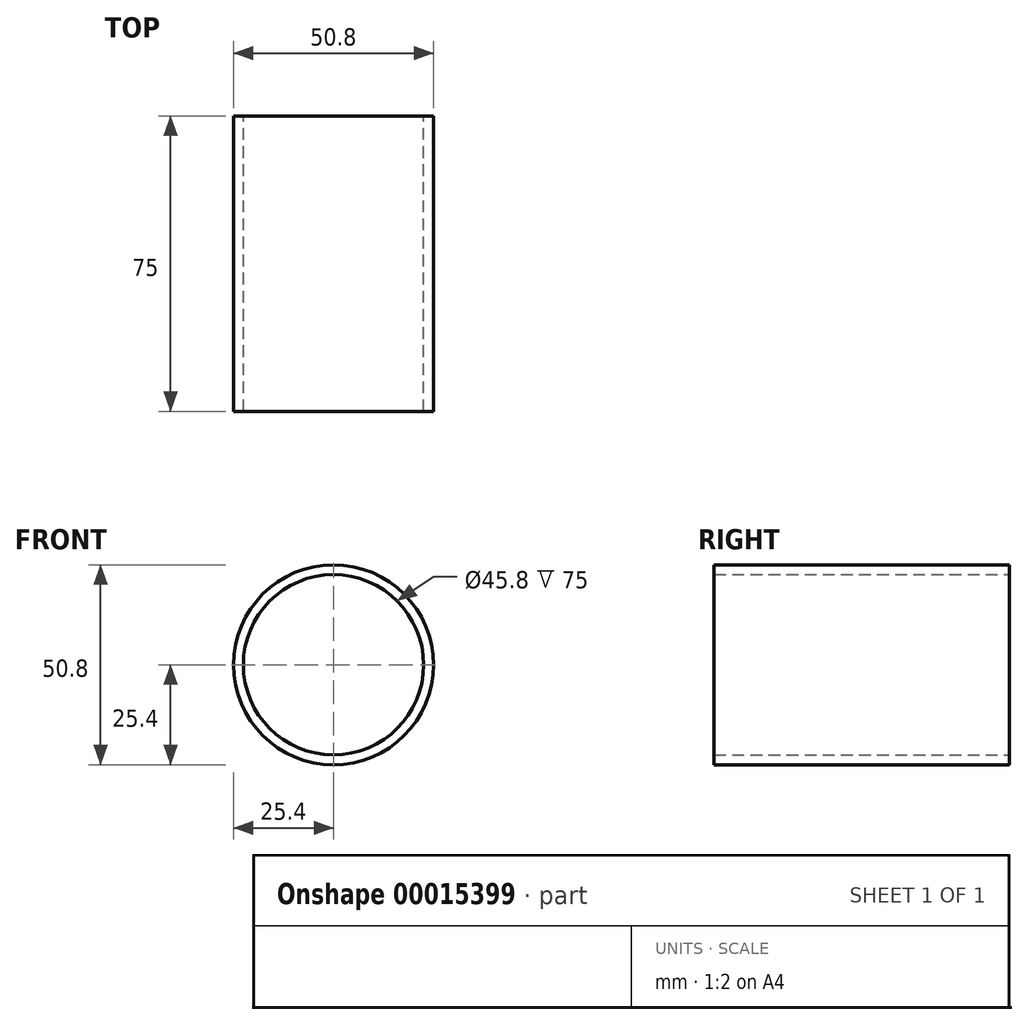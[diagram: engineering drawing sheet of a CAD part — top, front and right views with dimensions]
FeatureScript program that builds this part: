
annotation { "Feature Type Name" : "Feature", "Feature Type Description" : "" }
export const myFeature = defineFeature(function(context is Context, id is Id, definition is map)
    precondition{}
    {
        {
            var Q0;
            Q0=qCreatedBy(makeId("Front.planeOp"),FACE);
            var sketch = newSketch(context, id + "F0", { "sketchPlane" : qUnion([Q0])});
            skCircle(sketch, "E0", {"center": v(0, 0) * mm, "radius": 25.4 * mm});
            skSolve(sketch);
        }
        {
            var Q0;
            Q0=makeQuery(id+"F0.imprint","IMPRINT",FACE,{"disambiguationData":[TD([[makeQuery(id+"F0.imprint","IMPRINT",EDGE,{"derivedFrom":sQuery(id+"F0.wireOp",EDGE,"E0")}),1.0]])]});
            extrude(context, id + "F1", {"entities" : qUnion([Q0]), "depth" : 75 * mm});
        }
        {
            var Q0;
            Q0=makeQuery(id+"F1.opExtrude","CAP_FACE",FACE,{"disambiguationData":[OSD([sQuery(id+"F0.wireOp",EDGE,"E0")])],"isStart":false});
            var Q1;
            Q1=makeQuery(id+"F1.opExtrude","CAP_FACE",FACE,{"disambiguationData":[OSD([sQuery(id+"F0.wireOp",EDGE,"E0")])],"isStart":true});
            shell(context, id + "F2", {"entities" : qUnion([Q0, Q1]), "thickness" : 2.5 * mm});
        }
    });
